# Revit family: Distribution enclosure Marina cabinet glass door
name_source: partatom
category: Equipement électrique
units: mm (PartAtom-declared; Revit-internal decimal feet)

## family parameters
Basée sur le plan de construction = Non
Configuration du panneau = Deux colonnes, circuits au sein
Cote de connecteur circulaire = Utiliser le diamètre
Couper avec des vides une fois chargée = Non
Numéro OmniClass = 23.80.30.11.17
Partagée = Non
Point de calcul de pièce = Non
Titre OmniClass = Distribution Boards and Control Panels
Toujours verticalement = Oui
Type d'élément = Tableau de raccordement

## types (7) — shared parameters
ETIM Class 6.0 = EC000058
Fabricant = Legrand
General Conditions of Use = https://export.legrand.com
IK = 10
IP = 66
Image du type = Coffret_porte_vitree_036272_pw_92783_pz_14.jpg
Material = Polyester
RAL = 7035
URL = www.legrand.fr
zero-valued in all types: Elévation par défaut

## per-type parameters (varying)
| type | Cabinet 036271 | Cabinet 036272 | Cabinet 036275 | Cabinet 036276 | Cabinet 036281 | Cabinet 036283 | Cabinet 036284 | Description | depth | depth installation zone | distance before installation zone | distance side installation zone | height | weight | width | width installation zone |
| Marina cabinet glass door depth 206 height 400 width 300 | Oui | Non | Non | Non | Non | Non | Non | 036271  Marina cabinet glass door depth 206 height 400 width 300 | 206 mm  [stored 0.675853 ft] | 506 mm  [stored 1.6601 ft] | 300 mm  [stored 0.984252 ft] | 206 mm  [stored 0.675853 ft] | 400 mm  [stored 1.31234 ft] | 4.00 kg | 300 mm  [stored 0.984252 ft] | 712 mm  [stored 2.33596 ft] |
| Marina cabinet glass door depth 206 height 500 width 400 | Non | Oui | Non | Non | Non | Non | Non | 036272  Marina cabinet glass door depth 206 height 500 width 400 | 206 mm  [stored 0.675853 ft] | 606 mm  [stored 1.98819 ft] | 400 mm  [stored 1.31234 ft] | 206 mm  [stored 0.675853 ft] | 500 mm  [stored 1.64042 ft] | 5.60 kg | 400 mm  [stored 1.31234 ft] | 812 mm  [stored 2.66404 ft] |
| Marina cabinet glass door depth 257 height 610 width 400 | Non | Non | Oui | Non | Non | Non | Non | 036275  Marina cabinet glass door depth 257 height 610 width 400 | 257 mm  [stored 0.843176 ft] | 657 mm | 400 mm  [stored 1.31234 ft] | 257 mm  [stored 0.843176 ft] | 610 mm  [stored 2.00131 ft] | 7.00 kg | 400 mm  [stored 1.31234 ft] | 914 mm |
| Marina cabinet glass door depth 250 height 720 width 510 | Non | Non | Non | Oui | Non | Non | Non | 036276  Marina cabinet glass door depth 250 height 720 width 510 | 250 mm  [stored 0.82021 ft] | 760 mm  [stored 2.49344 ft] | 510 mm  [stored 1.67323 ft] | 250 mm  [stored 0.82021 ft] | 720 mm  [stored 2.3622 ft] | 12.30 kg | 510 mm  [stored 1.67323 ft] | 1010 mm  [stored 3.31365 ft] |
| Marina cabinet glass door depth 300 height 820 width 610 | Non | Non | Non | Non | Oui | Non | Non | 036281  Marina cabinet glass door depth 300 height 820 width 610 | 300 mm  [stored 0.984252 ft] | 910 mm | 610 mm  [stored 2.00131 ft] | 300 mm  [stored 0.984252 ft] | 820 mm  [stored 2.69029 ft] | 16.70 kg | 610 mm  [stored 2.00131 ft] | 1210 mm |
| Marina cabinet glass door depth 300 height 1020 width 810 | Non | Non | Non | Non | Non | Oui | Non | 036283  Marina cabinet glass door depth 300 height 1020 width 810 | 300 mm  [stored 0.984252 ft] | 1110 mm | 810 mm  [stored 2.65748 ft] | 300 mm  [stored 0.984252 ft] | 1020 mm  [stored 3.34646 ft] | 23.90 kg | 810 mm  [stored 2.65748 ft] | 1410 mm  [stored 4.62598 ft] |
| Marina cabinet glass door depth 300 height 1220 width 810 | Non | Non | Non | Non | Non | Non | Oui | 036284  Marina cabinet glass door depth 300 height 1220 width 810 | 300 mm  [stored 0.984252 ft] | 1110 mm | 810 mm  [stored 2.65748 ft] | 300 mm  [stored 0.984252 ft] | 1220 mm  [stored 4.00262 ft] | 27.50 kg | 810 mm  [stored 2.65748 ft] | 1410 mm  [stored 4.62598 ft] |

note: [stored X ft] marks values corroborated as IEEE doubles in the binary element streams (Revit-internal decimal feet)
